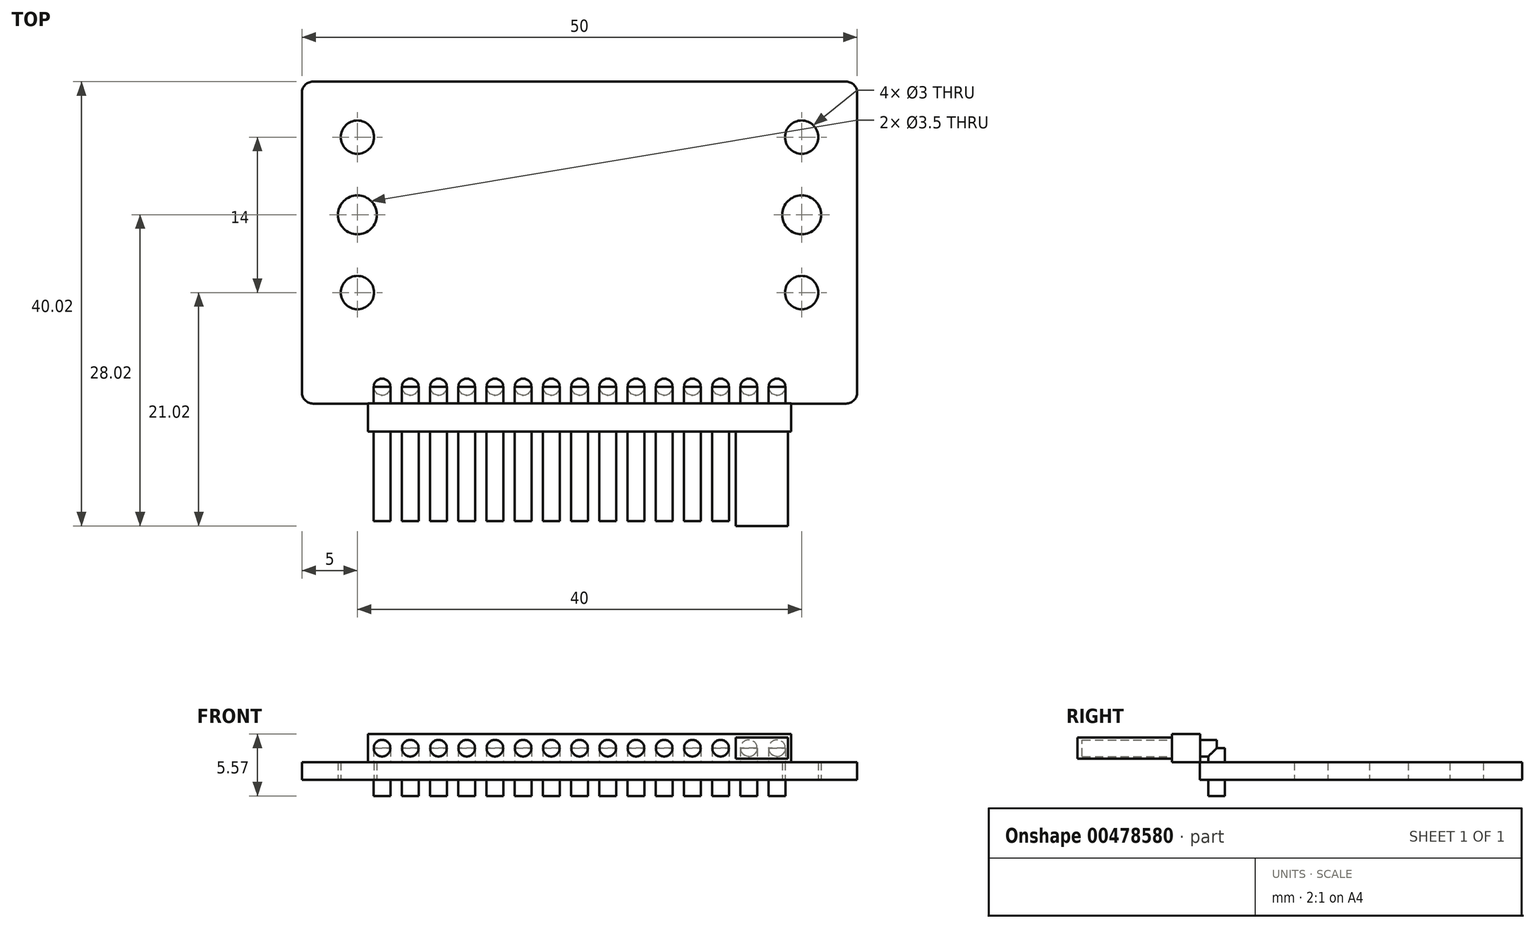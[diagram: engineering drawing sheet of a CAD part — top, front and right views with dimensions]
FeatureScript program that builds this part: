
annotation { "Feature Type Name" : "Feature", "Feature Type Description" : "" }
export const myFeature = defineFeature(function(context is Context, id is Id, definition is map)
    precondition{}
    {
        {
            var Q0;
            Q0=qCreatedBy(makeId("Top.planeOp"),FACE);
            var sketch = newSketch(context, id + "F0", { "sketchPlane" : qUnion([Q0])});
            skLineSegment(sketch, "E0.bottom", {"start": v(0, 0) * mm, "end": v(50, 0) * mm});
            skLineSegment(sketch, "E0.top", {"start": v(0, 29) * mm, "end": v(50, 29) * mm});
            skLineSegment(sketch, "E0.left", {"start": v(0, 0) * mm, "end": v(0, 29) * mm});
            skLineSegment(sketch, "E0.right", {"start": v(50, 0) * mm, "end": v(50, 29) * mm});
            skCircle(sketch, "E1", {"center": v(5, 17) * mm, "radius": 1.75 * mm});
            skCircle(sketch, "E2", {"center": v(5, 10) * mm, "radius": 1.5 * mm});
            skCircle(sketch, "E3", {"center": v(5, 24) * mm, "radius": 1.5 * mm});
            skLineSegment(sketch, "E4", {"start": v(5, 10) * mm, "end": v(5, 17) * mm, "construction": true});
            skLineSegment(sketch, "E5", {"start": v(5, 17) * mm, "end": v(5, 24) * mm, "construction": true});
            skLineSegment(sketch, "E6", {"start": v(25, 29) * mm, "end": v(25, 0) * mm, "construction": true});
            skCircle(sketch, "E7.MirrorC", {"center": v(45, 10) * mm, "radius": 1.5 * mm});
            skCircle(sketch, "E8.MirrorC", {"center": v(45, 17) * mm, "radius": 1.75 * mm});
            skCircle(sketch, "E9.MirrorC", {"center": v(45, 24) * mm, "radius": 1.5 * mm});
            skCircle(sketch, "E10", {"center": v(25, 1.5) * mm, "radius": 0.64 * mm});
            skCircle(sketch, "E11.1.0.0", {"center": v(27.54, 1.5) * mm, "radius": 0.64 * mm});
            skCircle(sketch, "E11.2.0.0", {"center": v(30.08, 1.5) * mm, "radius": 0.64 * mm});
            skCircle(sketch, "E11.3.0.0", {"center": v(32.62, 1.5) * mm, "radius": 0.64 * mm});
            skCircle(sketch, "E11.4.0.0", {"center": v(35.16, 1.5) * mm, "radius": 0.64 * mm});
            skCircle(sketch, "E11.5.0.0", {"center": v(37.7, 1.5) * mm, "radius": 0.64 * mm});
            skCircle(sketch, "E11.6.0.0", {"center": v(40.24, 1.5) * mm, "radius": 0.64 * mm});
            skLineSegment(sketch, "E11.direction1", {"start": v(25, 1.5) * mm, "end": v(27.54, 1.5) * mm, "construction": true});
            skCircle(sketch, "E12.1.0.0", {"center": v(22.46, 1.5) * mm, "radius": 0.64 * mm});
            skCircle(sketch, "E12.2.0.0", {"center": v(19.92, 1.5) * mm, "radius": 0.64 * mm});
            skCircle(sketch, "E12.3.0.0", {"center": v(17.38, 1.5) * mm, "radius": 0.64 * mm});
            skCircle(sketch, "E12.4.0.0", {"center": v(14.84, 1.5) * mm, "radius": 0.64 * mm});
            skCircle(sketch, "E12.5.0.0", {"center": v(12.3, 1.5) * mm, "radius": 0.64 * mm});
            skCircle(sketch, "E12.6.0.0", {"center": v(9.76, 1.5) * mm, "radius": 0.64 * mm});
            skLineSegment(sketch, "E12.direction1", {"start": v(25, 1.5) * mm, "end": v(22.46, 1.5) * mm, "construction": true});
            skCircle(sketch, "E13.0.7.0", {"center": v(42.78, 1.5) * mm, "radius": 0.64 * mm});
            skCircle(sketch, "E14.0.7.0", {"center": v(7.22, 1.5) * mm, "radius": 0.64 * mm});
            skSolve(sketch);
        }
        {
            var Q0;
            Q0 = qSketchRegion(id + "F0", true);
            extrude(context, id + "F1", {"entities" : qUnion([Q0]), "depth" : 1.6 * mm});
        }
        {
            var Q0;
            Q0=makeQuery(id+"F1.opExtrude","SWEPT_EDGE",EDGE,{"disambiguationData":[OSD([sQuery(id+"F0.wireOp",EDGE,"E0.bottom"),sQuery(id+"F0.wireOp",EDGE,"E0.left")])]});
            var Q1;
            Q1=makeQuery(id+"F1.opExtrude","SWEPT_EDGE",EDGE,{"disambiguationData":[OSD([sQuery(id+"F0.wireOp",EDGE,"E0.bottom"),sQuery(id+"F0.wireOp",EDGE,"E0.right")])]});
            var Q2;
            Q2=makeQuery(id+"F1.opExtrude","SWEPT_EDGE",EDGE,{"disambiguationData":[OSD([sQuery(id+"F0.wireOp",EDGE,"E0.top"),sQuery(id+"F0.wireOp",EDGE,"E0.right")])]});
            var Q3;
            Q3=makeQuery(id+"F1.opExtrude","SWEPT_EDGE",EDGE,{"disambiguationData":[OSD([sQuery(id+"F0.wireOp",EDGE,"E0.top"),sQuery(id+"F0.wireOp",EDGE,"E0.left")])]});
            fillet(context, id + "F2", {"entities" : qUnion([Q0, Q1, Q2, Q3]), "radius" : 1 * mm, "tangentPropagation" : true, "allowEdgeOverflow" : false});
        }
        {
            var Q0;
            Q0=makeQuery(id+"F1.opExtrude","CAP_FACE",FACE,{"disambiguationData":[OSD([sQuery(id+"F0.wireOp",EDGE,"E0.bottom"),sQuery(id+"F0.wireOp",EDGE,"E0.top"),sQuery(id+"F0.wireOp",EDGE,"E0.left"),sQuery(id+"F0.wireOp",EDGE,"E0.right"),sQuery(id+"F0.wireOp",EDGE,"E1"),sQuery(id+"F0.wireOp",EDGE,"E2"),sQuery(id+"F0.wireOp",EDGE,"E3"),sQuery(id+"F0.wireOp",EDGE,"E7.MirrorC"),sQuery(id+"F0.wireOp",EDGE,"E8.MirrorC"),sQuery(id+"F0.wireOp",EDGE,"E9.MirrorC"),sQuery(id+"F0.wireOp",EDGE,"McBm3XRj-A3Xa-I7OO-Wf4g-U8QMFdqaOmJE"),sQuery(id+"F0.wireOp",EDGE,"702775b5-039f-40cd-a728-acf4e70825b8.1.0.0"),sQuery(id+"F0.wireOp",EDGE,"702775b5-039f-40cd-a728-acf4e70825b8.2.0.0"),sQuery(id+"F0.wireOp",EDGE,"702775b5-039f-40cd-a728-acf4e70825b8.3.0.0"),sQuery(id+"F0.wireOp",EDGE,"702775b5-039f-40cd-a728-acf4e70825b8.4.0.0"),sQuery(id+"F0.wireOp",EDGE,"702775b5-039f-40cd-a728-acf4e70825b8.5.0.0"),sQuery(id+"F0.wireOp",EDGE,"702775b5-039f-40cd-a728-acf4e70825b8.6.0.0"),sQuery(id+"F0.wireOp",EDGE,"702775b5-039f-40cd-a728-acf4e70825b8.7.0.0")])],"isStart":false});
            var sketch = newSketch(context, id + "F3", { "sketchPlane" : qUnion([Q0])});
            skCircle(sketch, "E15", {"center": v(9.76, 1.5) * mm, "radius": 0.75 * mm});
            skCircle(sketch, "E16.1.0.0", {"center": v(12.3, 1.5) * mm, "radius": 0.75 * mm});
            skCircle(sketch, "E16.2.0.0", {"center": v(14.84, 1.5) * mm, "radius": 0.75 * mm});
            skCircle(sketch, "E16.3.0.0", {"center": v(17.38, 1.5) * mm, "radius": 0.75 * mm});
            skCircle(sketch, "E16.4.0.0", {"center": v(19.92, 1.5) * mm, "radius": 0.75 * mm});
            skCircle(sketch, "E16.5.0.0", {"center": v(22.46, 1.5) * mm, "radius": 0.75 * mm});
            skCircle(sketch, "E16.6.0.0", {"center": v(25, 1.5) * mm, "radius": 0.75 * mm});
            skCircle(sketch, "E16.7.0.0", {"center": v(27.54, 1.5) * mm, "radius": 0.75 * mm});
            skCircle(sketch, "E16.8.0.0", {"center": v(30.08, 1.5) * mm, "radius": 0.75 * mm});
            skCircle(sketch, "E16.9.0.0", {"center": v(32.62, 1.5) * mm, "radius": 0.75 * mm});
            skCircle(sketch, "E16.10.0.0", {"center": v(35.16, 1.5) * mm, "radius": 0.75 * mm});
            skCircle(sketch, "E16.11.0.0", {"center": v(37.7, 1.5) * mm, "radius": 0.75 * mm});
            skCircle(sketch, "E16.12.0.0", {"center": v(40.24, 1.5) * mm, "radius": 0.75 * mm});
            skLineSegment(sketch, "E16.direction1", {"start": v(9.76, 1.5) * mm, "end": v(12.3, 1.5) * mm, "construction": true});
            skCircle(sketch, "E17.0.13.0", {"center": v(42.78, 1.5) * mm, "radius": 0.75 * mm});
            skCircle(sketch, "E18.1.0.0", {"center": v(7.22, 1.5) * mm, "radius": 0.75 * mm});
            skLineSegment(sketch, "E18.direction1", {"start": v(9.76, 1.5) * mm, "end": v(7.22, 1.5) * mm, "construction": true});
            skSolve(sketch);
        }
        {
            var Q0;
            Q0 = qSketchRegion(id + "F3", true);
            extrude(context, id + "F4", {"entities" : qUnion([Q0]), "operationType" : NewBodyOperationType.ADD, "depth" : 1.25 * mm, "offsetDistance" : 25 * mm});
        }
        {
            var Q0;
            Q0 = qSketchRegion(id + "F3", true);
            extrude(context, id + "F5", {"entities" : qUnion([Q0]), "operationType" : NewBodyOperationType.ADD, "oppositeDirection" : true, "depth" : 3.05 * mm, "offsetDistance" : 25 * mm});
        }
        {
            var Q0;
            Q0=qCreatedBy(makeId("Front.planeOp"),FACE);
            cPlane(context, id + "F6", {"entities" : qUnion([Q0]), "cplaneType" : CPlaneType.OFFSET, "offset" : 1.5 * mm, "oppositeDirection" : true, "width" : 150 * mm, "height" : 150 * mm});
        }
        {
            var Q0;
            Q0=qCreatedBy(id+"F6.planeOp",FACE);
            var sketch = newSketch(context, id + "F7", { "sketchPlane" : qUnion([Q0])});
            skLineSegment(sketch, "E19.0", {"start": v(9, 2.85) * mm, "end": v(10.51, 2.85) * mm, "construction": true});
            skCircle(sketch, "E20", {"center": v(9.76, 2.85) * mm, "radius": 0.75 * mm});
            skCircle(sketch, "E21.1.0.0", {"center": v(12.3, 2.85) * mm, "radius": 0.75 * mm});
            skCircle(sketch, "E21.2.0.0", {"center": v(14.84, 2.85) * mm, "radius": 0.75 * mm});
            skCircle(sketch, "E21.3.0.0", {"center": v(17.38, 2.85) * mm, "radius": 0.75 * mm});
            skCircle(sketch, "E21.4.0.0", {"center": v(19.92, 2.85) * mm, "radius": 0.75 * mm});
            skCircle(sketch, "E21.5.0.0", {"center": v(22.46, 2.85) * mm, "radius": 0.75 * mm});
            skCircle(sketch, "E21.6.0.0", {"center": v(25, 2.85) * mm, "radius": 0.75 * mm});
            skCircle(sketch, "E21.7.0.0", {"center": v(27.54, 2.85) * mm, "radius": 0.75 * mm});
            skCircle(sketch, "E21.8.0.0", {"center": v(30.08, 2.85) * mm, "radius": 0.75 * mm});
            skCircle(sketch, "E21.9.0.0", {"center": v(32.62, 2.85) * mm, "radius": 0.75 * mm});
            skCircle(sketch, "E21.10.0.0", {"center": v(35.16, 2.85) * mm, "radius": 0.75 * mm});
            skCircle(sketch, "E21.11.0.0", {"center": v(37.7, 2.85) * mm, "radius": 0.75 * mm});
            skCircle(sketch, "E21.12.0.0", {"center": v(40.24, 2.85) * mm, "radius": 0.75 * mm});
            skLineSegment(sketch, "E21.direction1", {"start": v(9.76, 2.85) * mm, "end": v(12.3, 2.85) * mm, "construction": true});
            skCircle(sketch, "E22.0.13.0", {"center": v(42.78, 2.85) * mm, "radius": 0.75 * mm});
            skCircle(sketch, "E23.1.0.0", {"center": v(7.22, 2.85) * mm, "radius": 0.75 * mm});
            skLineSegment(sketch, "E23.direction1", {"start": v(9.76, 2.85) * mm, "end": v(7.22, 2.85) * mm, "construction": true});
            skSolve(sketch);
        }
        {
            var Q0;
            Q0 = qSketchRegion(id + "F7", true);
            extrude(context, id + "F8", {"entities" : qUnion([Q0]), "operationType" : NewBodyOperationType.ADD, "depth" : 12.1 * mm, "offsetDistance" : 25 * mm});
        }
        {
            var Q0;
            Q0=makeQuery(id+"F8.opExtrude","CAP_FACE",FACE,{"disambiguationData":[OSD([sQuery(id+"F7.wireOp",EDGE,"E20")])],"isStart":false});
            cPlane(context, id + "F9", {"entities" : qUnion([Q0]), "cplaneType" : CPlaneType.OFFSET, "offset" : 8.08 * mm, "oppositeDirection" : true, "width" : 150 * mm, "height" : 150 * mm});
        }
        {
            var Q0;
            Q0=qCreatedBy(id+"F9.planeOp",FACE);
            var sketch = newSketch(context, id + "F10", { "sketchPlane" : qUnion([Q0])});
            skLineSegment(sketch, "E24.bottom", {"start": v(5.95, 4.12) * mm, "end": v(44.05, 4.12) * mm});
            skLineSegment(sketch, "E24.top", {"start": v(5.95, 1.58) * mm, "end": v(44.05, 1.58) * mm});
            skLineSegment(sketch, "E24.left", {"start": v(5.95, 4.12) * mm, "end": v(5.95, 1.58) * mm});
            skLineSegment(sketch, "E24.right", {"start": v(44.05, 4.12) * mm, "end": v(44.05, 1.58) * mm});
            skLineSegment(sketch, "E25", {"start": v(7.22, 2.85) * mm, "end": v(5.95, 2.85) * mm, "construction": true});
            skCircle(sketch, "E26.0", {"center": v(7.22, 2.85) * mm, "radius": 0.75 * mm, "construction": true});
            skSolve(sketch);
        }
        {
            var Q0;
            Q0 = qSketchRegion(id + "F10", true);
            extrude(context, id + "F11", {"entities" : qUnion([Q0]), "operationType" : NewBodyOperationType.ADD, "oppositeDirection" : true, "depth" : 2.54 * mm, "offsetDistance" : 25 * mm});
        }
        {
            var Q0;
            Q0=makeQuery(id+"F11.opExtrude","CAP_FACE",FACE,{"disambiguationData":[OSD([sQuery(id+"F10.wireOp",EDGE,"E24.bottom"),sQuery(id+"F10.wireOp",EDGE,"E24.top"),sQuery(id+"F10.wireOp",EDGE,"E24.left"),sQuery(id+"F10.wireOp",EDGE,"E24.right")])],"isStart":true});
            var sketch = newSketch(context, id + "F12", { "sketchPlane" : qUnion([Q0])});
            skLineSegment(sketch, "E27.bottom", {"start": v(39.08, 3.8) * mm, "end": v(43.77, 3.8) * mm});
            skLineSegment(sketch, "E27.top", {"start": v(39.08, 1.9) * mm, "end": v(43.77, 1.9) * mm});
            skLineSegment(sketch, "E27.left", {"start": v(39.08, 3.8) * mm, "end": v(39.08, 1.9) * mm});
            skLineSegment(sketch, "E27.right", {"start": v(43.77, 3.8) * mm, "end": v(43.77, 1.9) * mm});
            skCircle(sketch, "E28.0", {"center": v(42.78, 2.85) * mm, "radius": 0.75 * mm, "construction": true});
            skLineSegment(sketch, "E29", {"start": v(42.78, 2.85) * mm, "end": v(43.77, 2.85) * mm, "construction": true});
            skSolve(sketch);
        }
        {
            var Q0;
            Q0 = qSketchRegion(id + "F12", true);
            extrude(context, id + "F13", {"entities" : qUnion([Q0]), "operationType" : NewBodyOperationType.ADD, "depth" : 8.5 * mm, "offsetDistance" : 25 * mm});
        }
    });
